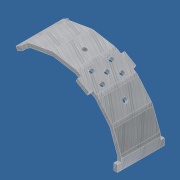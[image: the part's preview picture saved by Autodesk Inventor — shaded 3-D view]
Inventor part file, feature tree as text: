
AUTODESK INVENTOR PART (.ipt)
format: ipt  version: unknown  size: 297,472 bytes
history: native  units: in
note: dims shown in document units (in); Inventor stores cm internally (conversion verified against a paired STEP export)
features: extrude x4, sketch x3, mirror x2, fillet x1
ambient origin geometry x8: Origin, YZ Plane, XZ Plane, XY Plane, X Axis, Y Axis, Z Axis, Center Point
bodies: Solid1 (feature_tree)
feature tree (10):
  sketch  "Sketch1"  dims[d2=0.095in d8=0.095in]
  extrude  "Extrusion1"  Depth=0.095in
  extrude  "Extrusion2"  Depth=0.095in
  extrude  "Extrusion3"  Depth=0.1675in
  extrude  "Extrusion4"  Depth=0.1675in
  fillet  "Fillet1"  Radius=0.095in
  mirror  "Mirror5"
  mirror  "Mirror6"
  sketch  "Sketch2"  dims[d9=0.095in d10=0.095in]
  sketch  "Sketch3"  dims[d21=0.5in d22=0.0in d23=0.1675in d24=0.1675in d25=0.095in d26=0.0in d27=0.125in d28=0.095in d29=0.0in d30=0.125in d31=0.0in d32=0.125in d33=0.25in d34=0.1562in d35=0.095in d36=0.0in d37=0.25in d38=0.125in d41=3.25in d44=60.0deg]
